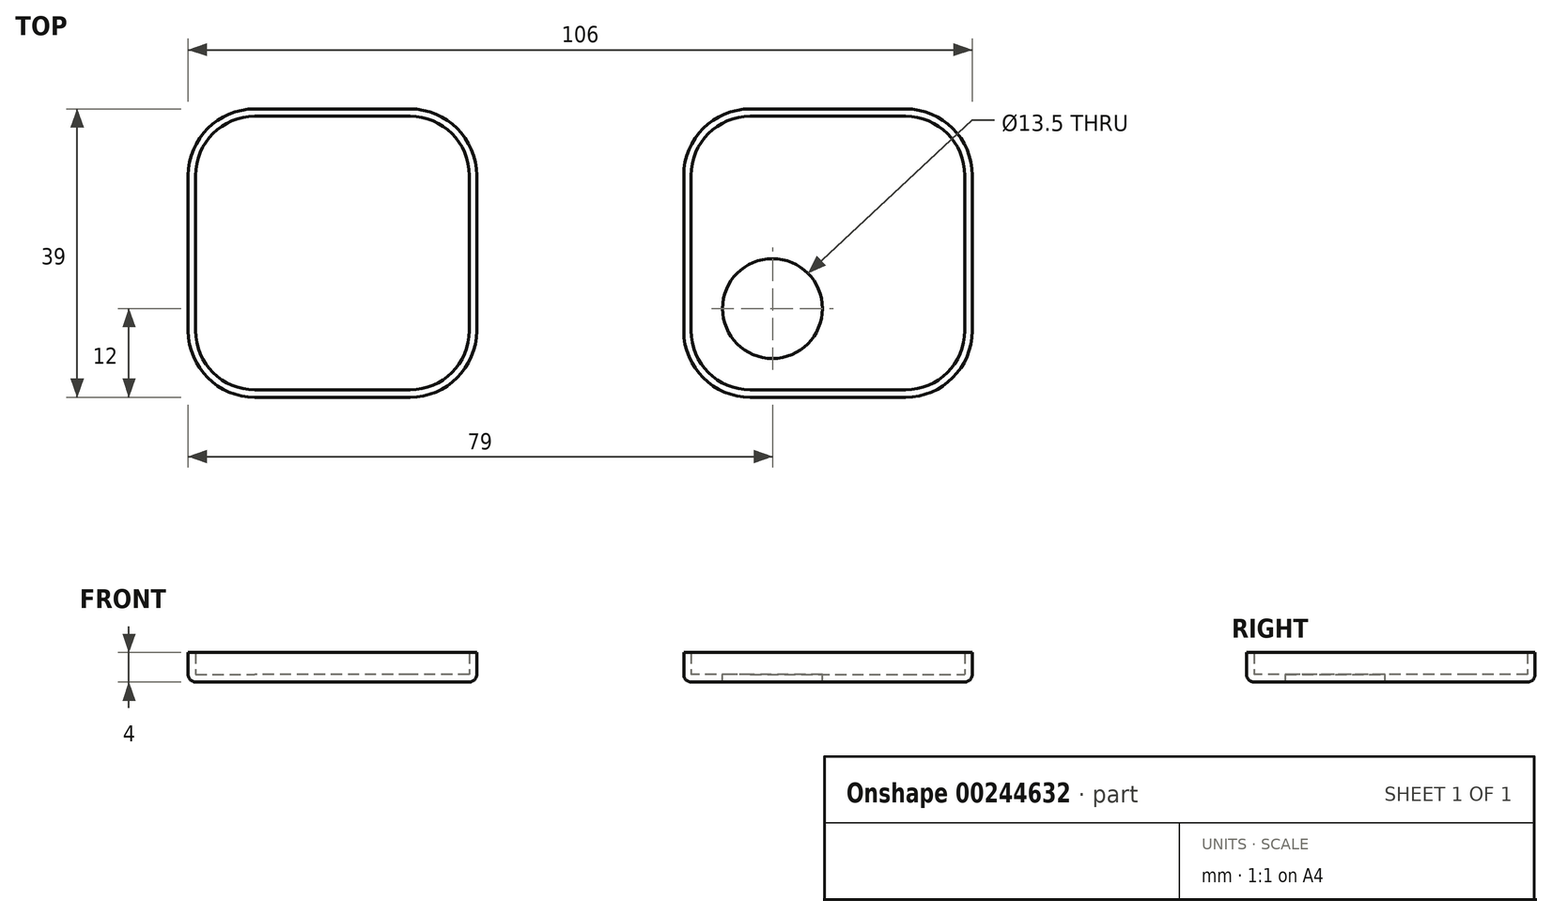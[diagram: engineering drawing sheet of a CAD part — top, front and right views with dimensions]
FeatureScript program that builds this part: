
annotation { "Feature Type Name" : "Feature", "Feature Type Description" : "" }
export const myFeature = defineFeature(function(context is Context, id is Id, definition is map)
    precondition{}
    {
        {
            var Q0;
            Q0=qCreatedBy(makeId("Top.planeOp"),FACE);
            var sketch = newSketch(context, id + "F0", { "sketchPlane" : qUnion([Q0])});
            skLineSegment(sketch, "E0.bottom", {"start": v(15, 18.5) * mm, "end": v(52, 18.5) * mm});
            skLineSegment(sketch, "E0.top", {"start": v(15, -18.5) * mm, "end": v(52, -18.5) * mm});
            skLineSegment(sketch, "E0.left", {"start": v(15, 18.5) * mm, "end": v(15, -18.5) * mm});
            skLineSegment(sketch, "E0.right", {"start": v(52, 18.5) * mm, "end": v(52, -18.5) * mm});
            skSolve(sketch);
        }
        {
            var Q0;
            Q0=makeQuery(id+"F0.imprint","IMPRINT",FACE,{"disambiguationData":[TD([[makeQuery(id+"F0.imprint","IMPRINT",EDGE,{"derivedFrom":sQuery(id+"F0.wireOp",EDGE,"E0.bottom")}),-1.0]])]});
            extrude(context, id + "F1", {"entities" : qUnion([Q0]), "depth" : 3 * mm});
        }
        {
            var Q0;
            Q0=makeQuery(id+"F1.opExtrude","SWEPT_EDGE",EDGE,{"disambiguationData":[OSD([sQuery(id+"F0.wireOp",EDGE,"E0.bottom"),sQuery(id+"F0.wireOp",EDGE,"E0.left")])]});
            var Q1;
            Q1=makeQuery(id+"F1.opExtrude","SWEPT_EDGE",EDGE,{"disambiguationData":[OSD([sQuery(id+"F0.wireOp",EDGE,"E0.bottom"),sQuery(id+"F0.wireOp",EDGE,"E0.right")])]});
            var Q2;
            Q2=makeQuery(id+"F1.opExtrude","SWEPT_EDGE",EDGE,{"disambiguationData":[OSD([sQuery(id+"F0.wireOp",EDGE,"E0.top"),sQuery(id+"F0.wireOp",EDGE,"E0.right")])]});
            var Q3;
            Q3=makeQuery(id+"F1.opExtrude","SWEPT_EDGE",EDGE,{"disambiguationData":[OSD([sQuery(id+"F0.wireOp",EDGE,"E0.top"),sQuery(id+"F0.wireOp",EDGE,"E0.left")])]});
            fillet(context, id + "F2", {"entities" : qUnion([Q0, Q1, Q2, Q3]), "radius" : 8 * mm, "tangentPropagation" : true, "allowEdgeOverflow" : false});
        }
        {
            var Q0;
            Q0=makeQuery(id+"F1.opExtrude","CAP_FACE",FACE,{"disambiguationData":[OSD([sQuery(id+"F0.wireOp",EDGE,"E0.bottom"),sQuery(id+"F0.wireOp",EDGE,"E0.top"),sQuery(id+"F0.wireOp",EDGE,"E0.left"),sQuery(id+"F0.wireOp",EDGE,"E0.right")])],"isStart":false});
            shell(context, id + "F3", {"entities" : qUnion([Q0]), "thickness" : 1 * mm, "oppositeDirection" : true});
        }
        {
            var Q0;
            Q0=makeQuery(id+"F1.opExtrude","CAP_FACE",FACE,{"disambiguationData":[OSD([sQuery(id+"F0.wireOp",EDGE,"E0.bottom"),sQuery(id+"F0.wireOp",EDGE,"E0.top"),sQuery(id+"F0.wireOp",EDGE,"E0.left"),sQuery(id+"F0.wireOp",EDGE,"E0.right")])],"isStart":true});
            fillet(context, id + "F4", {"entities" : qUnion([Q0]), "radius" : 1 * mm, "tangentPropagation" : true, "allowEdgeOverflow" : false});
        }
        {
            var Q0;
            Q0=makeQuery(id+"F1.opExtrude","SWEPT_BODY",BODY,{"disambiguationData":[OSD([sQuery(id+"F0.wireOp",EDGE,"E0.bottom"),sQuery(id+"F0.wireOp",EDGE,"E0.top"),sQuery(id+"F0.wireOp",EDGE,"E0.left"),sQuery(id+"F0.wireOp",EDGE,"E0.right")])]});
            var Q1;
            Q1=qCreatedBy(makeId("Right.planeOp"),FACE);
            mirror(context, id + "F5", {"entities" : qUnion([Q0]), "mirrorPlane" : qUnion([Q1])});
        }
        {
            var Q0;
            Q0=makeQuery(id+"F3.opShell","OFFSET_FACE",FACE,{"disambiguationData":[OSD([sQuery(id+"F0.wireOp",EDGE,"E0.bottom"),sQuery(id+"F0.wireOp",EDGE,"E0.top"),sQuery(id+"F0.wireOp",EDGE,"E0.left"),sQuery(id+"F0.wireOp",EDGE,"E0.right")])]});
            var sketch = newSketch(context, id + "F6", { "sketchPlane" : qUnion([Q0])});
            skCircle(sketch, "E1", {"center": v(26, -7.5) * mm, "radius": 6.75 * mm});
            skSolve(sketch);
        }
        {
            var Q0;
            Q0 = qSketchRegion(id + "F6", true);
            extrude(context, id + "F7", {"entities" : qUnion([Q0]), "operationType" : NewBodyOperationType.REMOVE, "endBound" : BoundingType.UP_TO_NEXT, "oppositeDirection" : true, "depth" : 25 * mm});
        }
    });
